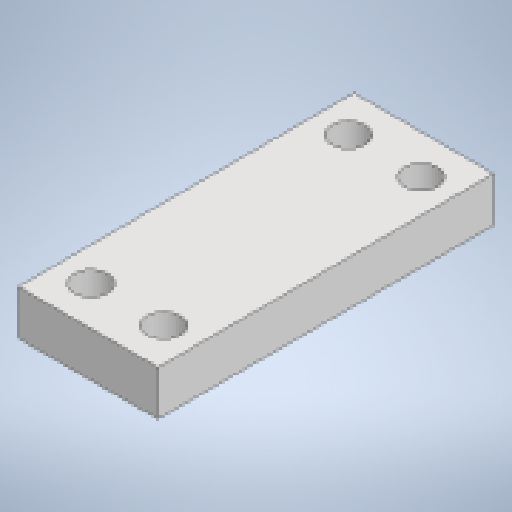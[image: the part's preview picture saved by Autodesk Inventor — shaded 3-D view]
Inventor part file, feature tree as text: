
AUTODESK INVENTOR PART (.ipt)
format: ipt  version: 2023 (Build 270158000, 158)  size: 141,312 bytes
history: native  units: mm
features: extrude x2, sketch x2, pattern_linear x1
ambient origin geometry x8: Origin, YZ Plane, XZ Plane, XY Plane, X Axis, Y Axis, Z Axis, Center Point
bodies: Solid1 (feature_tree)
feature tree (5):
  extrude  "Extrusion1"  Depth=8.0mm
  extrude  "Extrusion2"  Depth=25.0mm
  pattern_linear  "Rectangular Pattern1"  Spacing1=6.0mm  [1 undecoded]
  sketch  "Sketch1"  dims[d2=60.0mm d4=8.0mm]
  sketch  "Sketch2"  dims[d5=25.0mm d6=0.0mm d7=6.0mm d8=6.0mm d9=7.0mm d10=20.0mm d11=0.0mm d12=20.0mm d14=46.0mm d15=20.0mm d17=13.0mm]
note: 1 required parameter value undecoded (feature->parameter linkage not recoverable at this tier; creation-order binding heuristic only, values carry confidence <= 0.55)
